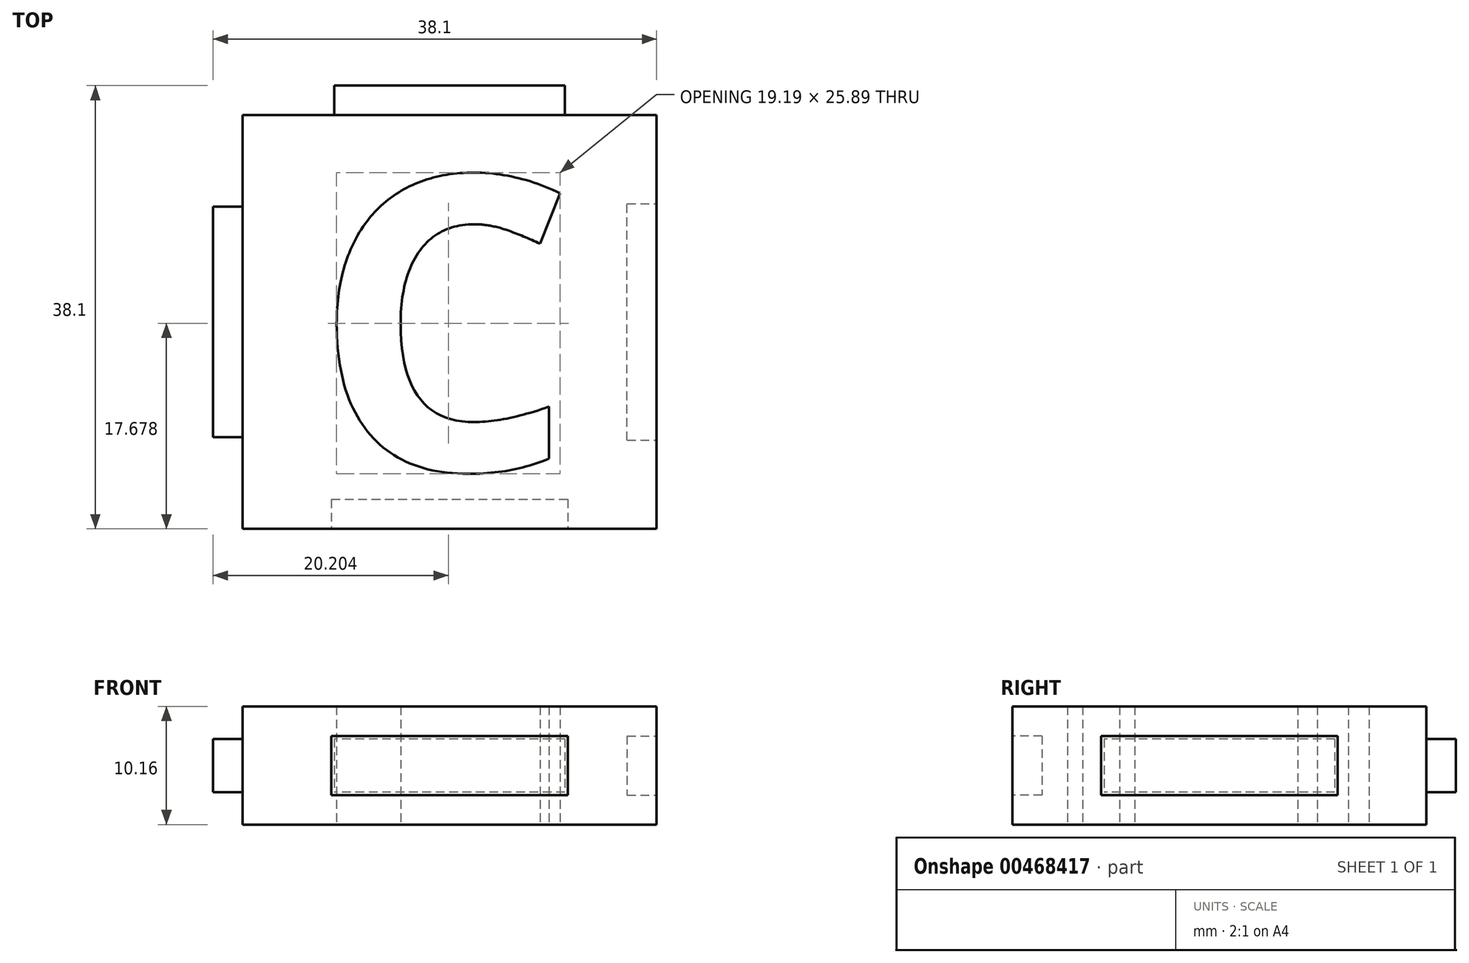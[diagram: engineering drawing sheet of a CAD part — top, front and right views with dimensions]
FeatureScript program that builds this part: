
annotation { "Feature Type Name" : "Feature", "Feature Type Description" : "" }
export const myFeature = defineFeature(function(context is Context, id is Id, definition is map)
    precondition{}
    {
        {
            var Q0;
            Q0=qCreatedBy(makeId("Top.planeOp"),FACE);
            var sketch = newSketch(context, id + "F0", { "sketchPlane" : qUnion([Q0])});
            skLineSegment(sketch, "E0.bottom", {"start": v(-17.78, 17.78) * mm, "end": v(17.78, 17.78) * mm});
            skLineSegment(sketch, "E0.top", {"start": v(-17.78, -17.78) * mm, "end": v(17.78, -17.78) * mm});
            skLineSegment(sketch, "E0.left", {"start": v(-17.78, 17.78) * mm, "end": v(-17.78, -17.78) * mm});
            skLineSegment(sketch, "E0.right", {"start": v(17.78, 17.78) * mm, "end": v(17.78, -17.78) * mm});
            skText(sketch, "E1", { "text": "C", "fontName": "OpenSans-Bold.ttf"});
            const initialGuessF0  = {"E1": [-0.01176, -0.0127, 1, 0, 0.0254]};
            skSetInitialGuess(sketch, initialGuessF0);
            skSolve(sketch);
        }
        {
            var Q0;
            Q0=qSketchRegion(id+"F0",true);
            extrude(context, id + "F1", {"entities" : qUnion([Q0]), "endBound" : BoundingType.SYMMETRIC, "depth" : 10.16 * mm});
        }
        {
            var Q0;
            Q0=makeQuery(id+"F1.opExtrude","SWEPT_FACE",FACE,{"disambiguationData":[OSD([sQuery(id+"F0.wireOp",EDGE,"E0.bottom")])]});
            var sketch = newSketch(context, id + "F2", { "sketchPlane" : qUnion([Q0])});
            skLineSegment(sketch, "E2.bottom", {"start": v(-9.9, 2.29) * mm, "end": v(9.9, 2.29) * mm});
            skLineSegment(sketch, "E2.top", {"start": v(-9.9, -2.29) * mm, "end": v(9.9, -2.29) * mm});
            skLineSegment(sketch, "E2.left", {"start": v(-9.9, 2.29) * mm, "end": v(-9.9, -2.29) * mm});
            skLineSegment(sketch, "E2.right", {"start": v(9.9, 2.29) * mm, "end": v(9.9, -2.29) * mm});
            skSolve(sketch);
        }
        {
            var Q0;
            Q0=qSketchRegion(id+"F2",true);
            extrude(context, id + "F3", {"entities" : qUnion([Q0]), "operationType" : NewBodyOperationType.ADD, "depth" : 2.54 * mm});
        }
        {
            var Q0;
            Q0=makeQuery(id+"F1.opExtrude","SWEPT_FACE",FACE,{"disambiguationData":[OSD([sQuery(id+"F0.wireOp",EDGE,"E0.left")])]});
            var sketch = newSketch(context, id + "F4", { "sketchPlane" : qUnion([Q0])});
            skLineSegment(sketch, "E3.bottom", {"start": v(-9.9, 2.29) * mm, "end": v(9.9, 2.29) * mm});
            skLineSegment(sketch, "E3.top", {"start": v(-9.9, -2.29) * mm, "end": v(9.9, -2.29) * mm});
            skLineSegment(sketch, "E3.left", {"start": v(-9.9, 2.29) * mm, "end": v(-9.9, -2.29) * mm});
            skLineSegment(sketch, "E3.right", {"start": v(9.9, 2.29) * mm, "end": v(9.9, -2.29) * mm});
            skSolve(sketch);
        }
        {
            var Q0;
            Q0=qSketchRegion(id+"F4",true);
            extrude(context, id + "F5", {"entities" : qUnion([Q0]), "operationType" : NewBodyOperationType.ADD, "depth" : 2.54 * mm});
        }
        {
            var Q0;
            Q0=makeQuery(id+"F1.opExtrude","SWEPT_FACE",FACE,{"disambiguationData":[OSD([sQuery(id+"F0.wireOp",EDGE,"E0.top")])]});
            var sketch = newSketch(context, id + "F6", { "sketchPlane" : qUnion([Q0])});
            skLineSegment(sketch, "E4.bottom", {"start": v(-10.16, 2.54) * mm, "end": v(10.16, 2.54) * mm});
            skLineSegment(sketch, "E4.top", {"start": v(-10.16, -2.54) * mm, "end": v(10.16, -2.54) * mm});
            skLineSegment(sketch, "E4.left", {"start": v(-10.16, 2.54) * mm, "end": v(-10.16, -2.54) * mm});
            skLineSegment(sketch, "E4.right", {"start": v(10.16, 2.54) * mm, "end": v(10.16, -2.54) * mm});
            skSolve(sketch);
        }
        {
            var Q0;
            Q0=qSketchRegion(id+"F6",true);
            extrude(context, id + "F7", {"entities" : qUnion([Q0]), "operationType" : NewBodyOperationType.REMOVE, "oppositeDirection" : true, "depth" : 2.54 * mm});
        }
        {
            var Q0;
            Q0=makeQuery(id+"F1.opExtrude","SWEPT_FACE",FACE,{"disambiguationData":[OSD([sQuery(id+"F0.wireOp",EDGE,"E0.right")])]});
            var sketch = newSketch(context, id + "F8", { "sketchPlane" : qUnion([Q0])});
            skLineSegment(sketch, "E5.bottom", {"start": v(-10.16, 2.54) * mm, "end": v(10.16, 2.54) * mm});
            skLineSegment(sketch, "E5.top", {"start": v(-10.16, -2.54) * mm, "end": v(10.16, -2.54) * mm});
            skLineSegment(sketch, "E5.left", {"start": v(-10.16, 2.54) * mm, "end": v(-10.16, -2.54) * mm});
            skLineSegment(sketch, "E5.right", {"start": v(10.16, 2.54) * mm, "end": v(10.16, -2.54) * mm});
            skSolve(sketch);
        }
        {
            var Q0;
            Q0=qSketchRegion(id+"F8",true);
            extrude(context, id + "F9", {"entities" : qUnion([Q0]), "operationType" : NewBodyOperationType.REMOVE, "oppositeDirection" : true, "depth" : 2.54 * mm});
        }
    });
